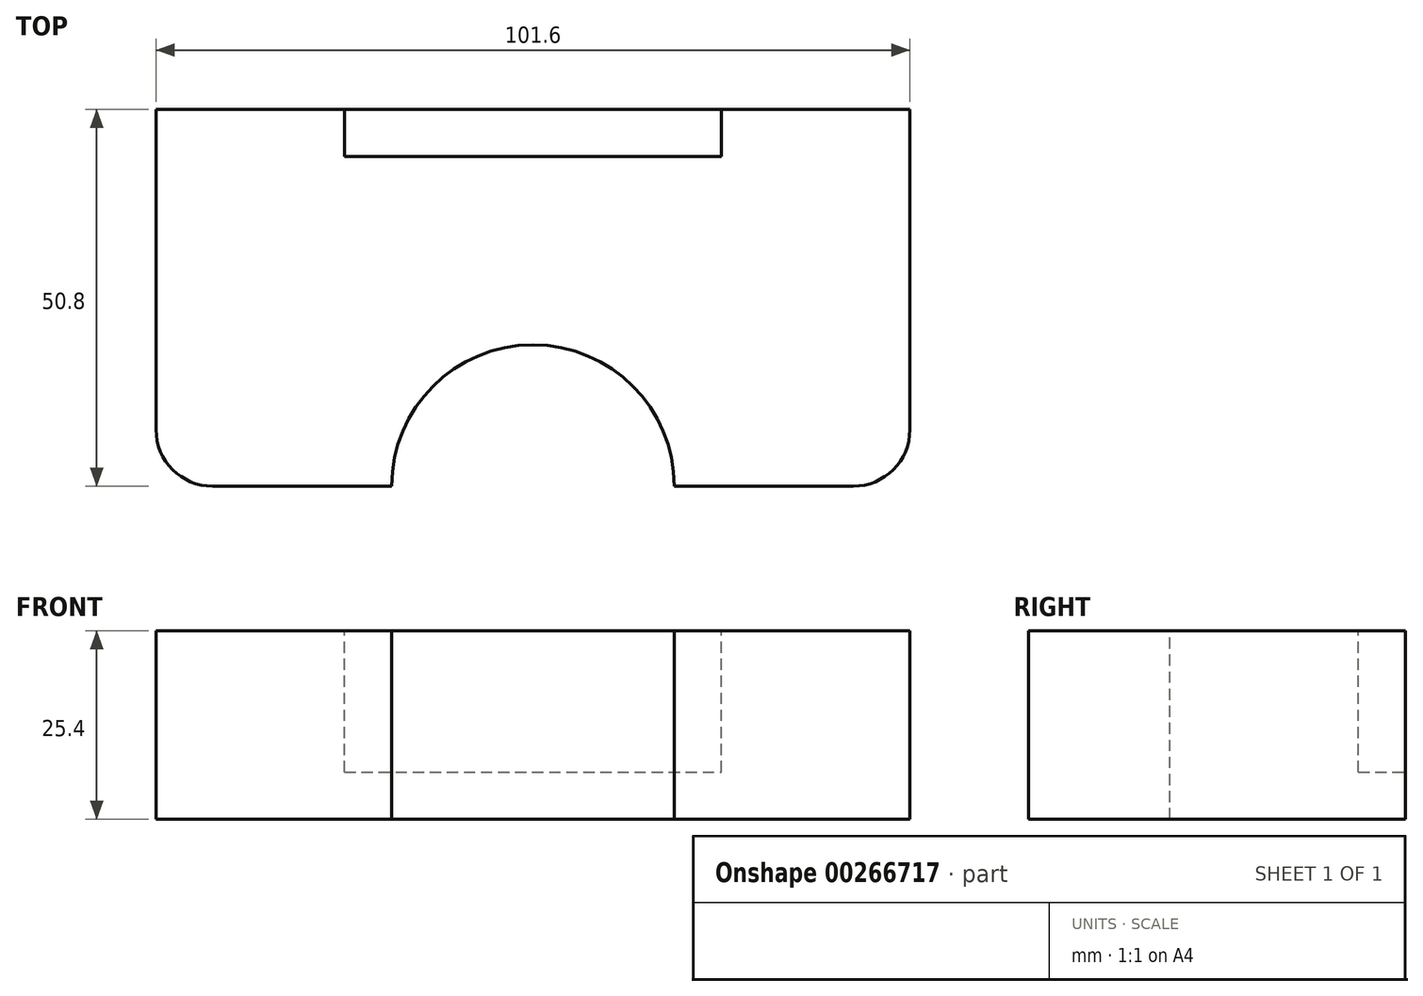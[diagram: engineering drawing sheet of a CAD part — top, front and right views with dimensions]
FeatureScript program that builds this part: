
annotation { "Feature Type Name" : "Feature", "Feature Type Description" : "" }
export const myFeature = defineFeature(function(context is Context, id is Id, definition is map)
    precondition{}
    {
        {
            var Q0;
            Q0=qCreatedBy(makeId("Top.planeOp"),FACE);
            var sketch = newSketch(context, id + "F0", { "sketchPlane" : qUnion([Q0])});
            skLineSegment(sketch, "E0.bottom", {"start": v(-50.8, 25.4) * mm, "end": v(50.8, 25.4) * mm});
            skLineSegment(sketch, "E0.top", {"start": v(-50.8, -25.4) * mm, "end": v(50.8, -25.4) * mm});
            skLineSegment(sketch, "E0.left", {"start": v(-50.8, 25.4) * mm, "end": v(-50.8, -25.4) * mm});
            skLineSegment(sketch, "E0.right", {"start": v(50.8, 25.4) * mm, "end": v(50.8, -25.4) * mm});
            skPoint(sketch, "E0.middle", {"position": v(0, 0) * mm});
            skSolve(sketch);
        }
        {
            var Q0;
            Q0=makeQuery(id+"F0.imprint","IMPRINT",FACE,{"disambiguationData":[TD([[makeQuery(id+"F0.imprint","IMPRINT",EDGE,{"derivedFrom":sQuery(id+"F0.wireOp",EDGE,"E0.bottom")}),-1.0]])]});
            extrude(context, id + "F1", {"entities" : qUnion([Q0]), "depth" : 25.4 * mm});
        }
        {
            var Q0;
            Q0=makeQuery(id+"F1.opExtrude","SWEPT_EDGE",EDGE,{"disambiguationData":[OSD([sQuery(id+"F0.wireOp",EDGE,"E0.top"),sQuery(id+"F0.wireOp",EDGE,"E0.left")])]});
            var Q1;
            Q1=makeQuery(id+"F1.opExtrude","SWEPT_EDGE",EDGE,{"disambiguationData":[OSD([sQuery(id+"F0.wireOp",EDGE,"E0.top"),sQuery(id+"F0.wireOp",EDGE,"E0.right")])]});
            fillet(context, id + "F2", {"entities" : qUnion([Q0, Q1]), "radius" : 7.62 * mm, "tangentPropagation" : true, "allowEdgeOverflow" : false});
        }
        {
            var Q0;
            Q0=makeQuery(id+"F1.opExtrude","CAP_FACE",FACE,{"disambiguationData":[OSD([sQuery(id+"F0.wireOp",EDGE,"E0.bottom"),sQuery(id+"F0.wireOp",EDGE,"E0.top"),sQuery(id+"F0.wireOp",EDGE,"E0.left"),sQuery(id+"F0.wireOp",EDGE,"E0.right")])],"isStart":false});
            var sketch = newSketch(context, id + "F3", { "sketchPlane" : qUnion([Q0])});
            skLineSegment(sketch, "E1.bottom", {"start": v(-25.4, 19.05) * mm, "end": v(25.4, 19.05) * mm});
            skLineSegment(sketch, "E1.top", {"start": v(-25.4, 25.4) * mm, "end": v(25.4, 25.4) * mm});
            skLineSegment(sketch, "E1.left", {"start": v(-25.4, 19.05) * mm, "end": v(-25.4, 25.4) * mm});
            skLineSegment(sketch, "E1.right", {"start": v(25.4, 19.05) * mm, "end": v(25.4, 25.4) * mm});
            skPoint(sketch, "E1.middle", {"position": v(0, 22.23) * mm});
            skSolve(sketch);
        }
        {
            var Q0;
            Q0=makeQuery(id+"F3.imprint","IMPRINT",FACE,{"disambiguationData":[TD([[makeQuery(id+"F3.imprint","IMPRINT",EDGE,{"derivedFrom":sQuery(id+"F3.wireOp",EDGE,"E1.bottom")}),1.0]])]});
            extrude(context, id + "F4", {"entities" : qUnion([Q0]), "operationType" : NewBodyOperationType.REMOVE, "oppositeDirection" : true, "depth" : 19.05 * mm});
        }
        {
            var Q0;
            Q0=makeQuery(id+"F1.opExtrude","CAP_FACE",FACE,{"disambiguationData":[OSD([sQuery(id+"F0.wireOp",EDGE,"E0.bottom"),sQuery(id+"F0.wireOp",EDGE,"E0.top"),sQuery(id+"F0.wireOp",EDGE,"E0.left"),sQuery(id+"F0.wireOp",EDGE,"E0.right")])],"isStart":false});
            var sketch = newSketch(context, id + "F5", { "sketchPlane" : qUnion([Q0])});
            skCircle(sketch, "E2", {"center": v(0, -25.4) * mm, "radius": 19.05 * mm});
            skSolve(sketch);
        }
        {
            var Q0;
            Q0 = qSketchRegion(id + "F5", true);
            extrude(context, id + "F6", {"entities" : qUnion([Q0]), "operationType" : NewBodyOperationType.REMOVE, "oppositeDirection" : true, "depth" : 25.4 * mm});
        }
    });
